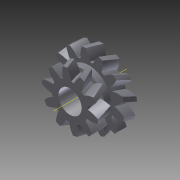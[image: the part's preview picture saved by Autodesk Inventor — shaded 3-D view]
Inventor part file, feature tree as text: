
AUTODESK INVENTOR PART (.ipt)
format: ipt  version: 2012 (Build 160160000, 160)  size: 591,360 bytes
history: native  units: in
note: dims shown in document units (in); Inventor stores cm internally (conversion verified against a paired STEP export)
features: other x5, extrude x3, sketch x3, projected_geometry x1, reference x1
ambient origin geometry x8: Origin, YZ Plane, XZ Plane, XY Plane, X Axis, Y Axis, Z Axis, Center Point
bodies: Solid1 (feature_tree)
feature tree (13):
  other  "LargeSmallTransferGear.iam"
  other  "BlankGearLargeAndSmall.ipt:1"
  other  "Spur Gear1:1"
  other  "Spur Gear2:1"
  extrude  "Extrusion1"  Depth=1.0in TaperAngle=0.0deg
  extrude  "Extrusion2"  Depth=0.0118in
  extrude  "Extrusion3"  [1 undecoded]
  other  "Work Axis1"
  sketch  "Sketch2"  dims[d0=0.3937in d1=1.0in d2=0.0in]
  projected_geometry  "Projected Loop1"
  sketch  "Sketch3"  dims[d3=1.0in d4=0.0in d6=0.0118in]
  sketch  "Sketch4"  dims[d7=0.3937in d8=0.0in]
  reference  "Reference1"
note: 1 required parameter value undecoded (feature->parameter linkage not recoverable at this tier; creation-order binding heuristic only, values carry confidence <= 0.55)
